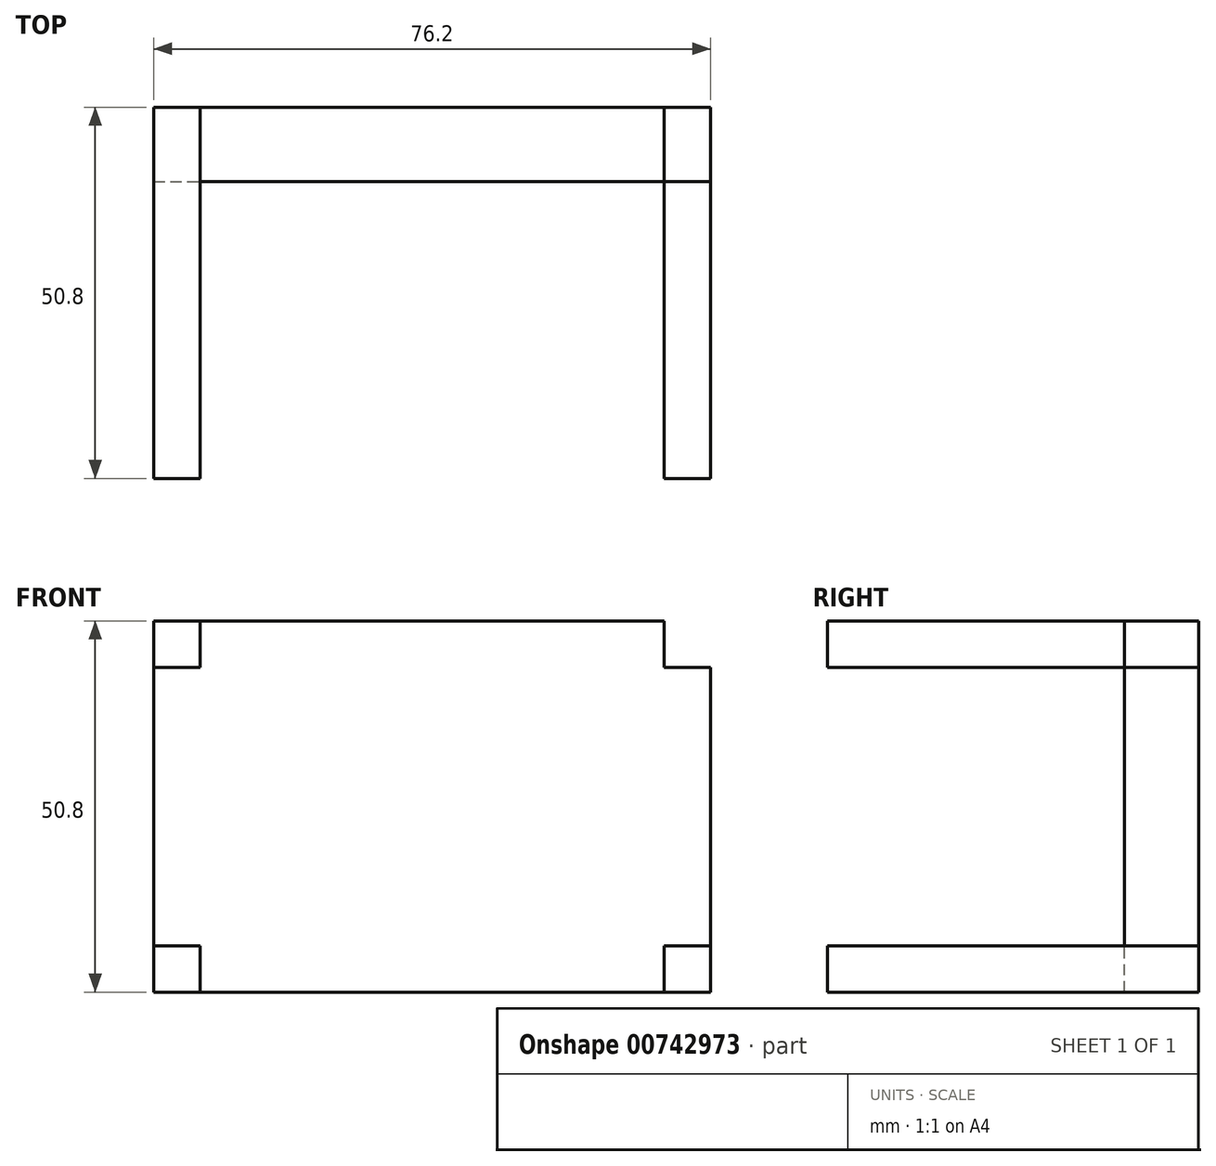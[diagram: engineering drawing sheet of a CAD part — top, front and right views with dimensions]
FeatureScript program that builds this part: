
annotation { "Feature Type Name" : "Feature", "Feature Type Description" : "" }
export const myFeature = defineFeature(function(context is Context, id is Id, definition is map)
    precondition{}
    {
        {
            var Q0;
            Q0=qCreatedBy(makeId("Front.planeOp"),FACE);
            var sketch = newSketch(context, id + "F0", { "sketchPlane" : qUnion([Q0])});
            skLineSegment(sketch, "E0.bottom", {"start": v(-34.47, 23.58) * mm, "end": v(-28.12, 23.58) * mm});
            skLineSegment(sketch, "E0.top", {"start": v(-34.47, 17.23) * mm, "end": v(-28.12, 17.23) * mm});
            skLineSegment(sketch, "E0.left", {"start": v(-34.47, 23.58) * mm, "end": v(-34.47, 17.23) * mm});
            skLineSegment(sketch, "E0.right", {"start": v(-28.12, 23.58) * mm, "end": v(-28.12, 17.23) * mm});
            skLineSegment(sketch, "E1.bottom", {"start": v(-34.47, 23.58) * mm, "end": v(41.73, 23.58) * mm});
            skLineSegment(sketch, "E1.left", {"start": v(-34.47, 23.58) * mm, "end": v(-34.47, -27.22) * mm});
            skLineSegment(sketch, "E2.bottom", {"start": v(41.73, 23.58) * mm, "end": v(35.38, 23.58) * mm});
            skLineSegment(sketch, "E2.top", {"start": v(41.73, 17.23) * mm, "end": v(35.38, 17.23) * mm});
            skLineSegment(sketch, "E2.left", {"start": v(41.73, 23.58) * mm, "end": v(41.73, 17.23) * mm});
            skLineSegment(sketch, "E2.right", {"start": v(35.38, 23.58) * mm, "end": v(35.38, 17.23) * mm});
            skLineSegment(sketch, "E3.bottom", {"start": v(-34.47, -27.22) * mm, "end": v(-28.12, -27.22) * mm});
            skLineSegment(sketch, "E3.top", {"start": v(-34.47, -20.87) * mm, "end": v(-28.12, -20.87) * mm});
            skLineSegment(sketch, "E3.left", {"start": v(-34.47, -27.22) * mm, "end": v(-34.47, -20.87) * mm});
            skLineSegment(sketch, "E3.right", {"start": v(-28.12, -27.22) * mm, "end": v(-28.12, -20.87) * mm});
            skLineSegment(sketch, "E4.bottom", {"start": v(41.73, -27.22) * mm, "end": v(35.38, -27.22) * mm});
            skLineSegment(sketch, "E4.top", {"start": v(41.73, -20.87) * mm, "end": v(35.38, -20.87) * mm});
            skLineSegment(sketch, "E4.left", {"start": v(41.73, -27.22) * mm, "end": v(41.73, -20.87) * mm});
            skLineSegment(sketch, "E4.right", {"start": v(35.38, -27.22) * mm, "end": v(35.38, -20.87) * mm});
            skLineSegment(sketch, "E5.bottom", {"start": v(-34.47, -27.22) * mm, "end": v(41.73, -27.22) * mm});
            skLineSegment(sketch, "E5.right", {"start": v(41.73, -27.22) * mm, "end": v(41.73, 23.58) * mm});
            skPoint(sketch, "E6.oppositeSnap0", {"position": v(41.73, 20.4) * mm});
            skSolve(sketch);
        }
        {
            var Q0;
            {var subQ0=sQuery(id+"F0.wireOp",EDGE,"E0.top");Q0=makeQuery(id+"F0.imprint","IMPRINT",FACE,{"disambiguationData":[TD([[makeQuery(id+"F0.imprint","IMPRINT",EDGE,{"derivedFrom":subQ0}),1.0]])]});}
            var Q1;
            {var subQ0=sQuery(id+"F0.wireOp",EDGE,"E2.bottom");Q1=makeQuery(id+"F0.imprint","IMPRINT",FACE,{"disambiguationData":[TD([[makeQuery(id+"F0.imprint","IMPRINT",EDGE,{"derivedFrom":subQ0}),1.0]])]});}
            var Q2;
            {var subQ0=sQuery(id+"F0.wireOp",EDGE,"E4.top");Q2=makeQuery(id+"F0.imprint","IMPRINT",FACE,{"disambiguationData":[TD([[makeQuery(id+"F0.imprint","IMPRINT",EDGE,{"derivedFrom":subQ0}),1.0]])]});}
            var Q3;
            Q3=makeQuery(id+"F0.imprint","IMPRINT",FACE,{"disambiguationData":[TD([[makeQuery(id+"F0.imprint","IMPRINT",EDGE,{"derivedFrom":sQuery(id+"F0.wireOp",EDGE,"E3.top")}),-1.0]])]});
            extrude(context, id + "F1", {"entities" : qUnion([Q0, Q1, Q2, Q3]), "depth" : 50.8 * mm, "offsetDistance" : 25.4 * mm});
        }
        {
            var Q0;
            {var subQ2=sQuery(id+"F0.wireOp",EDGE,"E0.top");Q0=makeQuery(id+"F0.imprint","IMPRINT",FACE,{"disambiguationData":[TD([[makeQuery(id+"F0.imprint","IMPRINT",EDGE,{"derivedFrom":subQ2}),-1.0]])]});}
            extrude(context, id + "F2", {"entities" : qUnion([Q0]), "depth" : 10.16 * mm, "offsetDistance" : 25.4 * mm});
        }
    });
